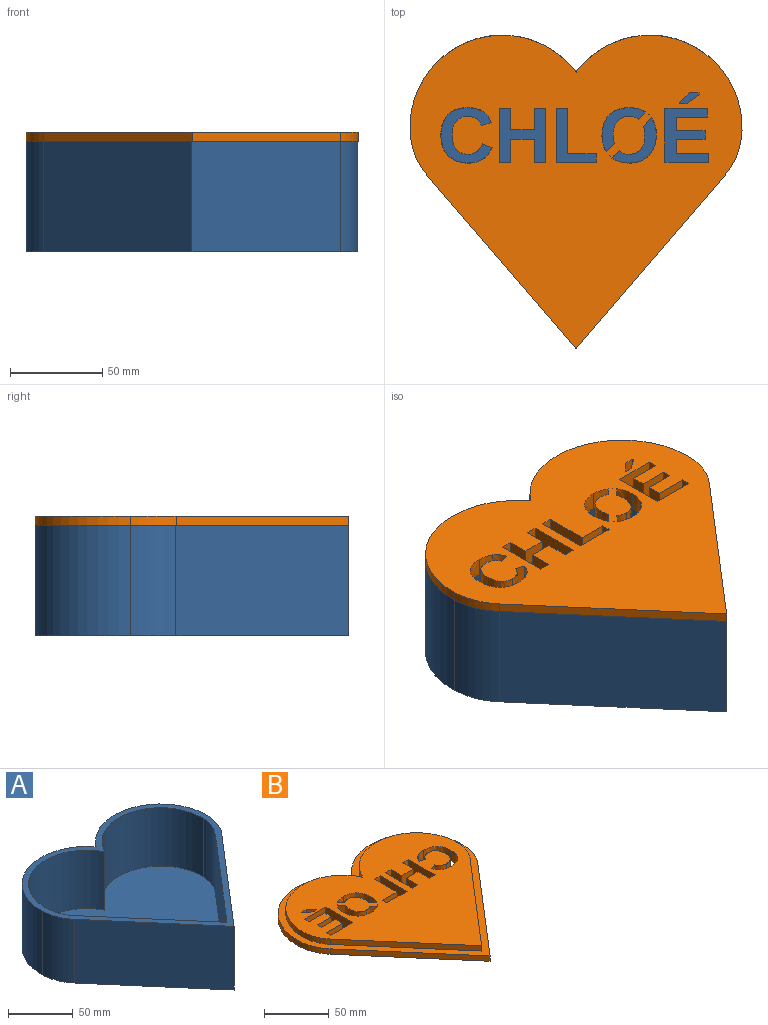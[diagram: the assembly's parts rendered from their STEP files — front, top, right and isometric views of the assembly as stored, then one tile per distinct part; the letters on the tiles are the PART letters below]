
ASSEMBLY  parts=2 mates=1
PART A: 15 faces, bbox 180x170x60 mm
  f0: cylinder r=50mm len=90mm, axis (0,0,-1), area 7593.7mm2, adj f1,f4,f5,f7
  f1: cylinder r=50mm len=90mm, axis (0,0,-1), area 7593.7mm2, adj f0,f4,f5,f6
  f2: plane 93.62x80.35mm, normal (-0.76,-0.65,0), area 7402.2mm2, adj f3,f4,f5,f6
  f3: plane 93.62x80.35mm, normal (0.76,-0.65,0), area 7402.2mm2, adj f2,f4,f5,f7
  f4: plane 180x170mm, normal (0,0,1), area 2696.4mm2, adj f0,f1,f2,f3,f6,f7,f8,f9
  f5: plane 180x170mm, normal (0,0,-1), area 19557.2mm2, adj f0,f1,f2,f3,f6,f7
  f6: cylinder r=40mm len=60mm, axis (0,0,-1), area 1622.7mm2, adj f1,f2,f4,f5
  f7: cylinder r=40mm len=60mm, axis (0,0,-1), area 1622.7mm2, adj f0,f3,f4,f5
  f8: cylinder r=45mm len=85mm, axis (0,0,-1), area 6679.6mm2, adj f4,f9,f12,f14
  f9: cylinder r=45mm len=85mm, axis (0,0,-1), area 6679.6mm2, adj f4,f8,f12,f13
  f10: plane 89.2x76.55mm, normal (0.76,0.65,0), area 6464.9mm2, adj f4,f11,f12,f13
  f11: plane 89.2x76.55mm, normal (-0.76,0.65,0), area 6464.9mm2, adj f4,f10,f12,f14
  f12: plane 170x157.32mm, normal (0,0,1), area 16860.8mm2, adj f8,f9,f10,f11,f13,f14
  f13: cylinder r=35mm len=55mm, axis (0,0,-1), area 1301.6mm2, adj f4,f9,f10,f12
  f14: cylinder r=35mm len=55mm, axis (0,0,-1), area 1301.6mm2, adj f4,f8,f11,f12
PART B: 93 faces, bbox 180x170x10 mm
  f0: extruded ~10x0.31mm, area 4.3mm2, adj f2,f3,f87
  f1: extruded ~10x9.29mm, area 98.6mm2, adj f2,f3,f60,f90
  f2: plane 180x170mm, normal (0,0,-1), area 17691.9mm2, adj f0,f1,f4,f5,f6,f7,f9,f10
  f3: plane 168x154.79mm, normal (0,0,1), area 14472.7mm2, adj f0,f1,f11,f12,f13,f14,f15,f16
  f4: cylinder r=50mm len=90mm, axis (0,0,-1), area 632.8mm2, adj f2,f5,f8,f10
  f5: cylinder r=50mm len=90mm, axis (0,0,-1), area 632.8mm2, adj f2,f4,f8,f9
  f6: plane 93.62x80.35mm, normal (-0.76,-0.65,0), area 616.8mm2, adj f2,f7,f8,f9
  f7: plane 93.62x80.35mm, normal (0.76,-0.65,0), area 616.8mm2, adj f2,f6,f8,f10
  f8: plane 180x170mm, normal (0,0,1), area 3219.2mm2, adj f4,f5,f6,f7,f9,f10,f11,f12
  f9: cylinder r=40mm len=24.73mm, axis (0,0,-1), area 135.2mm2, adj f2,f5,f6,f8
  f10: cylinder r=40mm len=24.73mm, axis (0,0,-1), area 135.2mm2, adj f2,f4,f7,f8
  f11: cylinder r=44mm len=84mm, axis (0,0,-1), area 603.9mm2, adj f3,f8,f12,f16
  f12: cylinder r=44mm len=84mm, axis (0,0,-1), area 603.9mm2, adj f3,f8,f11,f13
  f13: cylinder r=34mm len=21.02mm, axis (0,0,-1), area 114.9mm2, adj f3,f8,f12,f14
  f14: plane 88.31x75.8mm, normal (-0.76,-0.65,0), area 581.9mm2, adj f3,f8,f13,f15
  f15: plane 88.31x75.8mm, normal (0.76,-0.65,0), area 581.9mm2, adj f3,f8,f14,f16
  f16: cylinder r=34mm len=21.02mm, axis (0,0,-1), area 114.9mm2, adj f3,f8,f11,f15
  f17: plane 12.53x10mm, normal (-1,0,0), area 125.3mm2, adj f2,f3,f18,f28
  f18: plane 10x6.12mm, normal (0,1,0), area 61.2mm2, adj f2,f3,f17,f19
  f19: plane 29.23x10mm, normal (1,0,0), area 292.3mm2, adj f2,f3,f18,f20
  f20: plane 10x6.12mm, normal (0,-1,0), area 61.2mm2, adj f2,f3,f19,f21
  f21: plane 11.64x10mm, normal (-1,0,0), area 116.4mm2, adj f2,f3,f20,f22
  f22: plane 12.74x10mm, normal (0,-1,0), area 127.4mm2, adj f2,f3,f21,f23
  f23: plane 11.64x10mm, normal (1,0,0), area 116.4mm2, adj f2,f3,f22,f24
  f24: plane 10x6.12mm, normal (0,-1,0), area 61.2mm2, adj f2,f3,f23,f25
  f25: plane 29.23x10mm, normal (-1,0,0), area 292.3mm2, adj f2,f3,f24,f26
  f26: plane 10x6.12mm, normal (0,1,0), area 61.2mm2, adj f2,f3,f25,f27
  f27: plane 12.53x10mm, normal (1,0,0), area 125.3mm2, adj f2,f3,f26,f28
  f28: plane 12.74x10mm, normal (0,1,0), area 127.4mm2, adj f2,f3,f17,f27
  f29: plane 29.23x10mm, normal (-1,0,0), area 292.3mm2, adj f2,f3,f30,f34
  f30: plane 21.81x10mm, normal (0,1,0), area 218.1mm2, adj f2,f3,f29,f31
  f31: plane 10x4.73mm, normal (1,0,0), area 47.3mm2, adj f2,f3,f30,f32
  f32: plane 15.69x10mm, normal (0,-1,0), area 156.9mm2, adj f2,f3,f31,f33
  f33: plane 24.5x10mm, normal (1,0,0), area 245mm2, adj f2,f3,f32,f34
  f34: plane 10x6.12mm, normal (0,-1,0), area 61.2mm2, adj f2,f3,f29,f33
  f35: plane 29.23x10mm, normal (-1,0,0), area 292.3mm2, adj f2,f3,f36,f46
  f36: plane 23.84x10mm, normal (0,1,0), area 238.4mm2, adj f2,f3,f35,f37
  f37: plane 10x4.73mm, normal (1,0,0), area 47.3mm2, adj f2,f3,f36,f38
  f38: plane 17.72x10mm, normal (0,-1,0), area 177.2mm2, adj f2,f3,f37,f39
  f39: plane 10x7.69mm, normal (1,0,0), area 76.9mm2, adj f2,f3,f38,f40
  f40: plane 15.6x10mm, normal (0,1,0), area 156mm2, adj f2,f3,f39,f41
  f41: plane 10x4.73mm, normal (1,0,0), area 47.3mm2, adj f2,f3,f40,f42
  f42: plane 15.6x10mm, normal (0,-1,0), area 156mm2, adj f2,f3,f41,f43
  f43: plane 10x7.35mm, normal (1,0,0), area 73.5mm2, adj f2,f3,f42,f44
  f44: plane 16.87x10mm, normal (0,1,0), area 168.7mm2, adj f2,f3,f43,f45
  f45: plane 10x4.73mm, normal (1,0,0), area 47.3mm2, adj f2,f3,f44,f46
  f46: plane 22.99x10mm, normal (0,-1,0), area 229.9mm2, adj f2,f3,f35,f45
  f47: plane 10x0.64mm, normal (-1,0,0), area 6.4mm2, adj f2,f3,f48,f52
  f48: plane 10x3.53mm, normal (0,1,0), area 35.3mm2, adj f2,f3,f47,f49
  f49: plane 10x7.06mm, normal (0.58,0.81,0), area 86.6mm2, adj f2,f3,f48,f50
  f50: plane 10x0.89mm, normal (1,0,0), area 8.9mm2, adj f2,f3,f49,f51
  f51: plane 10x5.36mm, normal (0,-1,0), area 53.6mm2, adj f2,f3,f50,f52
  f52: plane 10x5.27mm, normal (-0.71,-0.7,0), area 74.2mm2, adj f2,f3,f47,f51
  f53: extruded ~10x8.03mm, area 83.1mm2, adj f2,f3,f54,f61
  f54: extruded ~10x9.39mm, area 99.1mm2, adj f2,f3,f53,f89
  f55: extruded ~10x8.92mm, area 93.7mm2, adj f2,f3,f56,f88
  f56: extruded ~10.84x10mm, area 118.6mm2, adj f2,f3,f55,f57
  f57: extruded ~10.97x10mm, area 119.6mm2, adj f2,f3,f56,f58
  f58: extruded ~10x9.12mm, area 95.5mm2, adj f2,f3,f57,f91
  f59: extruded ~10x0.48mm, area 6.7mm2, adj f2,f3,f92
  f60: extruded ~10x7.84mm, area 81.4mm2, adj f1,f2,f3,f61
  f61: extruded ~10x5.3mm, area 75.1mm2, adj f2,f3,f53,f60
  f62: extruded ~10x7.7mm, area 101.9mm2, adj f2,f3,f63,f78
  f63: extruded ~10x6.38mm, area 71.5mm2, adj f2,f3,f62,f64
  f64: extruded ~10x7.69mm, area 81.7mm2, adj f2,f3,f63,f65
  f65: extruded ~10x7.53mm, area 79.9mm2, adj f2,f3,f64,f66
  f66: extruded ~10x6.3mm, area 70.4mm2, adj f2,f3,f65,f67
  f67: extruded ~10x4.72mm, area 49.6mm2, adj f2,f3,f66,f68
  f68: extruded ~10x3.5mm, area 45mm2, adj f2,f3,f67,f69
  f69: plane 10x5.4mm, normal (0.26,0.96,0), area 56mm2, adj f2,f3,f68,f70
  f70: extruded ~10x6.07mm, area 77.4mm2, adj f2,f3,f69,f71
  f71: extruded ~10x8.38mm, area 87.5mm2, adj f2,f3,f70,f72
  f72: extruded ~10.77x10mm, area 117.7mm2, adj f2,f3,f71,f73
  f73: extruded ~11.06x10mm, area 119.6mm2, adj f2,f3,f72,f74
  f74: extruded ~11.17x10mm, area 121.2mm2, adj f2,f3,f73,f75
  f75: extruded ~10.9x10mm, area 119.4mm2, adj f2,f3,f74,f76
  f76: extruded ~10x7.98mm, area 83.5mm2, adj f2,f3,f75,f77
  f77: extruded ~10x6.3mm, area 82.2mm2, adj f2,f3,f76,f78
  f78: plane 10x5.33mm, normal (0.35,-0.94,0), area 57mm2, adj f2,f3,f62,f77
  f79: extruded ~10x5.04mm, area 53.5mm2, adj f2,f3,f80,f88
  f80: extruded ~10x6.34mm, area 71.2mm2, adj f2,f3,f79,f81
  f81: extruded ~10x7.44mm, area 79.3mm2, adj f2,f3,f80,f82
  f82: extruded ~10x4.57mm, area 46.4mm2, adj f2,f3,f81,f91
  f83: extruded ~10x5.39mm, area 58.4mm2, adj f2,f3,f84,f90
  f84: extruded ~10x6.34mm, area 71.3mm2, adj f2,f3,f83,f85
  f85: extruded ~10x7.65mm, area 81.3mm2, adj f2,f3,f84,f86
  f86: extruded ~10x4.91mm, area 50mm2, adj f2,f3,f85,f89
  f87: plane 10x0.31mm, normal (-0.7,0.71,0), area 4.3mm2, adj f0,f2,f3
  f88: plane 10x3.94mm, normal (0.71,0.7,0), area 55.3mm2, adj f2,f3,f55,f79
  f89: plane 10x4.49mm, normal (-0.71,-0.7,0), area 62.9mm2, adj f2,f3,f54,f86
  f90: plane 10x3.97mm, normal (-0.71,-0.7,0), area 55.6mm2, adj f1,f2,f3,f83
  f91: plane 10x4.55mm, normal (0.71,0.7,0), area 63.8mm2, adj f2,f3,f58,f82
  f92: plane 10x0.48mm, normal (0.7,-0.71,0), area 6.7mm2, adj f2,f3,f59
PLACE A at identity fixed
PLACE B rot(axis=(0,1,0),180deg) t=(0,-0.09,65)mm
MATE fastened B.f8 <-> A.f4  axis (0,0,-1) through (0,-17.36,60)mm
